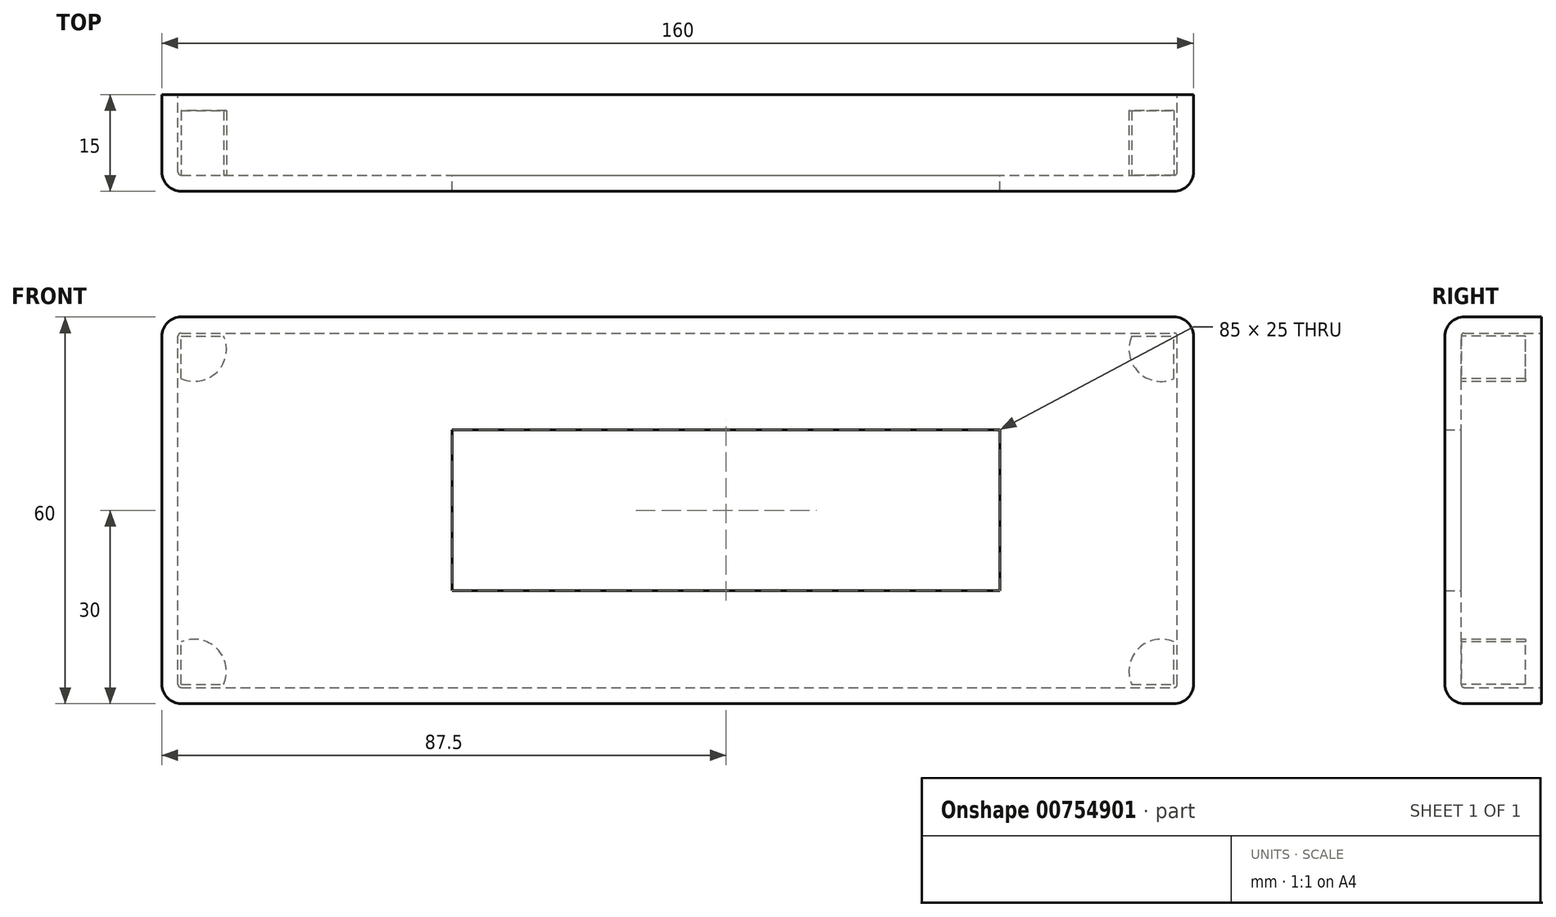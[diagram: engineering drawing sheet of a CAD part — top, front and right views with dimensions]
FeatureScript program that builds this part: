
annotation { "Feature Type Name" : "Feature", "Feature Type Description" : "" }
export const myFeature = defineFeature(function(context is Context, id is Id, definition is map)
    precondition{}
    {
        {
            var Q0;
            Q0=qCreatedBy(makeId("Front.planeOp"),FACE);
            var sketch = newSketch(context, id + "F0", { "sketchPlane" : qUnion([Q0])});
            skLineSegment(sketch, "E0.bottom", {"start": v(0, 0) * mm, "end": v(160, 0) * mm});
            skLineSegment(sketch, "E0.top", {"start": v(0, 60) * mm, "end": v(160, 60) * mm});
            skLineSegment(sketch, "E0.left", {"start": v(0, 0) * mm, "end": v(0, 60) * mm});
            skLineSegment(sketch, "E0.right", {"start": v(160, 0) * mm, "end": v(160, 60) * mm});
            skSolve(sketch);
        }
        {
            var Q0;
            Q0=makeQuery(id+"F0.imprint","IMPRINT",FACE,{"disambiguationData":[TD([[makeQuery(id+"F0.imprint","IMPRINT",EDGE,{"derivedFrom":sQuery(id+"F0.wireOp",EDGE,"E0.bottom")}),1.0]])]});
            extrude(context, id + "F1", {"entities" : qUnion([Q0]), "depth" : 15 * mm, "offsetDistance" : 25 * mm});
        }
        {
            var Q0;
            Q0=makeQuery(id+"F1.opExtrude","SWEPT_EDGE",EDGE,{"disambiguationData":[OSD([sQuery(id+"F0.wireOp",EDGE,"E0.top"),sQuery(id+"F0.wireOp",EDGE,"E0.left")])]});
            var Q1;
            Q1=makeQuery(id+"F1.opExtrude","CAP_EDGE",EDGE,{"disambiguationData":[OSD([sQuery(id+"F0.wireOp",EDGE,"E0.top")])],"isStart":false});
            var Q2;
            Q2=makeQuery(id+"F1.opExtrude","CAP_EDGE",EDGE,{"disambiguationData":[OSD([sQuery(id+"F0.wireOp",EDGE,"E0.left")])],"isStart":false});
            var Q3;
            Q3=makeQuery(id+"F1.opExtrude","CAP_EDGE",EDGE,{"disambiguationData":[OSD([sQuery(id+"F0.wireOp",EDGE,"E0.bottom")])],"isStart":false});
            var Q4;
            Q4=makeQuery(id+"F1.opExtrude","SWEPT_EDGE",EDGE,{"disambiguationData":[OSD([sQuery(id+"F0.wireOp",EDGE,"E0.bottom"),sQuery(id+"F0.wireOp",EDGE,"E0.left")])]});
            var Q5;
            Q5=makeQuery(id+"F1.opExtrude","SWEPT_EDGE",EDGE,{"disambiguationData":[OSD([sQuery(id+"F0.wireOp",EDGE,"E0.bottom"),sQuery(id+"F0.wireOp",EDGE,"E0.right")])]});
            var Q6;
            Q6=makeQuery(id+"F1.opExtrude","SWEPT_EDGE",EDGE,{"disambiguationData":[OSD([sQuery(id+"F0.wireOp",EDGE,"E0.top"),sQuery(id+"F0.wireOp",EDGE,"E0.right")])]});
            var Q7;
            Q7=makeQuery(id+"F1.opExtrude","CAP_EDGE",EDGE,{"disambiguationData":[OSD([sQuery(id+"F0.wireOp",EDGE,"E0.right")])],"isStart":false});
            fillet(context, id + "F2", {"entities" : qUnion([Q0, Q1, Q2, Q3, Q4, Q5, Q6, Q7]), "radius" : 3 * mm, "tangentPropagation" : true, "allowEdgeOverflow" : false});
        }
        {
            var Q0;
            Q0=makeQuery(id+"F1.opExtrude","CAP_FACE",FACE,{"disambiguationData":[OSD([sQuery(id+"F0.wireOp",EDGE,"E0.bottom"),sQuery(id+"F0.wireOp",EDGE,"E0.top"),sQuery(id+"F0.wireOp",EDGE,"E0.left"),sQuery(id+"F0.wireOp",EDGE,"E0.right")])],"isStart":true});
            shell(context, id + "F3", {"entities" : qUnion([Q0]), "thickness" : 2.5 * mm});
        }
        {
            var Q0;
            Q0=makeQuery(id+"F3.opShell","OFFSET_FACE",FACE,{"disambiguationData":[OSD([sQuery(id+"F0.wireOp",EDGE,"E0.bottom"),sQuery(id+"F0.wireOp",EDGE,"E0.top"),sQuery(id+"F0.wireOp",EDGE,"E0.left"),sQuery(id+"F0.wireOp",EDGE,"E0.right")])]});
            var sketch = newSketch(context, id + "F4", { "sketchPlane" : qUnion([Q0])});
            skCircle(sketch, "E1", {"center": v(-155, 55) * mm, "radius": 5 * mm});
            skCircle(sketch, "E2", {"center": v(-155, 5) * mm, "radius": 5 * mm});
            skCircle(sketch, "E3", {"center": v(-5, 55) * mm, "radius": 5 * mm});
            skCircle(sketch, "E4", {"center": v(-5, 5) * mm, "radius": 5 * mm});
            skSolve(sketch);
        }
        {
            var Q0;
            {var subQ0=sQuery(id+"F4.wireOp",EDGE,"E1");var subQ1=sQuery(id+"F0.wireOp",EDGE,"E0.right");var subQ2=sQuery(id+"F0.wireOp",EDGE,"E0.left");var subQ3=sQuery(id+"F0.wireOp",EDGE,"E0.top");var subQ4=sQuery(id+"F0.wireOp",EDGE,"E0.bottom");var subQ5=makeQuery(id+"F1.opExtrude","CAP_FACE",FACE,{"disambiguationData":[OSD([subQ4,subQ3,subQ2,subQ1])],"isStart":false});var subQ6=makeQuery(id+"F3.opShell","OFFSET_EDGE",EDGE,{"disambiguationData":[OSD([subQ4,subQ3,subQ2,subQ1]),TDD([makeQuery(id+"F2.opFillet","BLEND_EDGE",EDGE,{"blendedFrom":[makeQuery(id+"F1.opExtrude","CAP_EDGE",EDGE,{"disambiguationData":[OSD([subQ3])],"isStart":false}),subQ5],"blendedInto":[subQ5]})])]});var subQ7=makeQuery(id+"F4.imprint","INTERSECT",VERTEX,{"derivedFrom":[subQ6,subQ0]});Q0=makeQuery(id+"F4.imprint","IMPRINT",FACE,{"disambiguationData":[TD([[makeQuery(id+"F4.imprint","IMPRINT",EDGE,{"disambiguationData":[TD([[subQ7,1.0]])],"derivedFrom":subQ0}),1.0]])]});}
            var Q1;
            {var subQ0=sQuery(id+"F4.wireOp",EDGE,"E2");var subQ1=sQuery(id+"F0.wireOp",EDGE,"E0.right");var subQ2=sQuery(id+"F0.wireOp",EDGE,"E0.left");var subQ3=sQuery(id+"F0.wireOp",EDGE,"E0.top");var subQ4=sQuery(id+"F0.wireOp",EDGE,"E0.bottom");var subQ5=makeQuery(id+"F1.opExtrude","CAP_FACE",FACE,{"disambiguationData":[OSD([subQ4,subQ3,subQ2,subQ1])],"isStart":false});var subQ6=makeQuery(id+"F3.opShell","OFFSET_EDGE",EDGE,{"disambiguationData":[OSD([subQ4,subQ3,subQ2,subQ1]),TDD([makeQuery(id+"F2.opFillet","BLEND_EDGE",EDGE,{"blendedFrom":[makeQuery(id+"F1.opExtrude","CAP_EDGE",EDGE,{"disambiguationData":[OSD([subQ4])],"isStart":false}),subQ5],"blendedInto":[subQ5]})])]});var subQ7=makeQuery(id+"F4.imprint","INTERSECT",VERTEX,{"derivedFrom":[subQ6,subQ0]});Q1=makeQuery(id+"F4.imprint","IMPRINT",FACE,{"disambiguationData":[TD([[makeQuery(id+"F4.imprint","IMPRINT",EDGE,{"disambiguationData":[TD([[subQ7,-1.0]])],"derivedFrom":subQ0}),1.0]])]});}
            var Q2;
            {var subQ0=sQuery(id+"F4.wireOp",EDGE,"E3");var subQ1=sQuery(id+"F0.wireOp",EDGE,"E0.right");var subQ2=sQuery(id+"F0.wireOp",EDGE,"E0.left");var subQ3=sQuery(id+"F0.wireOp",EDGE,"E0.top");var subQ4=sQuery(id+"F0.wireOp",EDGE,"E0.bottom");var subQ5=makeQuery(id+"F1.opExtrude","CAP_FACE",FACE,{"disambiguationData":[OSD([subQ4,subQ3,subQ2,subQ1])],"isStart":false});var subQ6=makeQuery(id+"F3.opShell","OFFSET_EDGE",EDGE,{"disambiguationData":[OSD([subQ4,subQ3,subQ2,subQ1]),TDD([makeQuery(id+"F2.opFillet","BLEND_EDGE",EDGE,{"blendedFrom":[makeQuery(id+"F1.opExtrude","CAP_EDGE",EDGE,{"disambiguationData":[OSD([subQ3])],"isStart":false}),subQ5],"blendedInto":[subQ5]})])]});var subQ7=makeQuery(id+"F4.imprint","INTERSECT",VERTEX,{"derivedFrom":[subQ6,subQ0]});Q2=makeQuery(id+"F4.imprint","IMPRINT",FACE,{"disambiguationData":[TD([[makeQuery(id+"F4.imprint","IMPRINT",EDGE,{"disambiguationData":[TD([[subQ7,-1.0]])],"derivedFrom":subQ0}),1.0]])]});}
            var Q3;
            {var subQ0=sQuery(id+"F4.wireOp",EDGE,"E4");var subQ1=sQuery(id+"F0.wireOp",EDGE,"E0.right");var subQ2=sQuery(id+"F0.wireOp",EDGE,"E0.left");var subQ3=sQuery(id+"F0.wireOp",EDGE,"E0.top");var subQ4=sQuery(id+"F0.wireOp",EDGE,"E0.bottom");var subQ5=makeQuery(id+"F1.opExtrude","CAP_FACE",FACE,{"disambiguationData":[OSD([subQ4,subQ3,subQ2,subQ1])],"isStart":false});var subQ6=makeQuery(id+"F3.opShell","OFFSET_EDGE",EDGE,{"disambiguationData":[OSD([subQ4,subQ3,subQ2,subQ1]),TDD([makeQuery(id+"F2.opFillet","BLEND_EDGE",EDGE,{"blendedFrom":[makeQuery(id+"F1.opExtrude","CAP_EDGE",EDGE,{"disambiguationData":[OSD([subQ4])],"isStart":false}),subQ5],"blendedInto":[subQ5]})])]});var subQ7=makeQuery(id+"F4.imprint","INTERSECT",VERTEX,{"derivedFrom":[subQ6,subQ0]});Q3=makeQuery(id+"F4.imprint","IMPRINT",FACE,{"disambiguationData":[TD([[makeQuery(id+"F4.imprint","IMPRINT",EDGE,{"disambiguationData":[TD([[subQ7,1.0]])],"derivedFrom":subQ0}),1.0]])]});}
            var Q4;
            {var subQ0=sQuery(id+"F4.wireOp",EDGE,"ceb6a8c3-83ea-4a42-8ad1-0d2410ddc587");var subQ1=sQuery(id+"F0.wireOp",EDGE,"E0.right");var subQ2=sQuery(id+"F0.wireOp",EDGE,"E0.left");var subQ3=sQuery(id+"F0.wireOp",EDGE,"E0.top");var subQ4=sQuery(id+"F0.wireOp",EDGE,"E0.bottom");var subQ5=makeQuery(id+"F1.opExtrude","CAP_FACE",FACE,{"disambiguationData":[OSD([subQ4,subQ3,subQ2,subQ1])],"isStart":false});var subQ6=makeQuery(id+"F3.opShell","OFFSET_EDGE",EDGE,{"disambiguationData":[OSD([subQ4,subQ3,subQ2,subQ1]),TDD([makeQuery(id+"F2.opFillet","BLEND_EDGE",EDGE,{"blendedFrom":[makeQuery(id+"F1.opExtrude","CAP_EDGE",EDGE,{"disambiguationData":[OSD([subQ3])],"isStart":false}),subQ5],"blendedInto":[subQ5]})])]});var subQ7=makeQuery(id+"F4.imprint","INTERSECT",VERTEX,{"derivedFrom":[subQ6,subQ0]});Q4=makeQuery(id+"F4.imprint","IMPRINT",FACE,{"disambiguationData":[TD([[makeQuery(id+"F4.imprint","IMPRINT",EDGE,{"disambiguationData":[TD([[subQ7,1.0]])],"derivedFrom":subQ0}),-1.0]])]});}
            var Q5;
            {var subQ0=sQuery(id+"F4.wireOp",EDGE,"14a948d3-5733-4252-9dd9-3c15a1e3127a");var subQ1=sQuery(id+"F0.wireOp",EDGE,"E0.right");var subQ2=sQuery(id+"F0.wireOp",EDGE,"E0.left");var subQ3=sQuery(id+"F0.wireOp",EDGE,"E0.top");var subQ4=sQuery(id+"F0.wireOp",EDGE,"E0.bottom");var subQ5=makeQuery(id+"F1.opExtrude","CAP_FACE",FACE,{"disambiguationData":[OSD([subQ4,subQ3,subQ2,subQ1])],"isStart":false});var subQ6=makeQuery(id+"F3.opShell","OFFSET_EDGE",EDGE,{"disambiguationData":[OSD([subQ4,subQ3,subQ2,subQ1]),TDD([makeQuery(id+"F2.opFillet","BLEND_EDGE",EDGE,{"blendedFrom":[makeQuery(id+"F1.opExtrude","CAP_EDGE",EDGE,{"disambiguationData":[OSD([subQ3])],"isStart":false}),subQ5],"blendedInto":[subQ5]})])]});var subQ7=makeQuery(id+"F4.imprint","INTERSECT",VERTEX,{"derivedFrom":[subQ6,subQ0]});Q5=makeQuery(id+"F4.imprint","IMPRINT",FACE,{"disambiguationData":[TD([[makeQuery(id+"F4.imprint","IMPRINT",EDGE,{"disambiguationData":[TD([[subQ7,-1.0]])],"derivedFrom":subQ0}),-1.0]])]});}
            var Q6;
            {var subQ0=sQuery(id+"F4.wireOp",EDGE,"e6a02f4f-9173-470f-86b5-5cf8c1340213");var subQ1=sQuery(id+"F0.wireOp",EDGE,"E0.right");var subQ2=sQuery(id+"F0.wireOp",EDGE,"E0.left");var subQ3=sQuery(id+"F0.wireOp",EDGE,"E0.top");var subQ4=sQuery(id+"F0.wireOp",EDGE,"E0.bottom");var subQ5=makeQuery(id+"F1.opExtrude","CAP_FACE",FACE,{"disambiguationData":[OSD([subQ4,subQ3,subQ2,subQ1])],"isStart":false});var subQ6=makeQuery(id+"F3.opShell","OFFSET_EDGE",EDGE,{"disambiguationData":[OSD([subQ4,subQ3,subQ2,subQ1]),TDD([makeQuery(id+"F2.opFillet","BLEND_EDGE",EDGE,{"blendedFrom":[makeQuery(id+"F1.opExtrude","CAP_EDGE",EDGE,{"disambiguationData":[OSD([subQ4])],"isStart":false}),subQ5],"blendedInto":[subQ5]})])]});var subQ7=makeQuery(id+"F4.imprint","INTERSECT",VERTEX,{"derivedFrom":[subQ6,subQ0]});Q6=makeQuery(id+"F4.imprint","IMPRINT",FACE,{"disambiguationData":[TD([[makeQuery(id+"F4.imprint","IMPRINT",EDGE,{"disambiguationData":[TD([[subQ7,1.0]])],"derivedFrom":subQ0}),-1.0]])]});}
            var Q7;
            {var subQ0=sQuery(id+"F4.wireOp",EDGE,"3f37ad98-5e16-4e9e-b798-fc5b4a82ff59");var subQ1=sQuery(id+"F0.wireOp",EDGE,"E0.right");var subQ2=sQuery(id+"F0.wireOp",EDGE,"E0.left");var subQ3=sQuery(id+"F0.wireOp",EDGE,"E0.top");var subQ4=sQuery(id+"F0.wireOp",EDGE,"E0.bottom");var subQ5=makeQuery(id+"F1.opExtrude","CAP_FACE",FACE,{"disambiguationData":[OSD([subQ4,subQ3,subQ2,subQ1])],"isStart":false});var subQ6=makeQuery(id+"F3.opShell","OFFSET_EDGE",EDGE,{"disambiguationData":[OSD([subQ4,subQ3,subQ2,subQ1]),TDD([makeQuery(id+"F2.opFillet","BLEND_EDGE",EDGE,{"blendedFrom":[makeQuery(id+"F1.opExtrude","CAP_EDGE",EDGE,{"disambiguationData":[OSD([subQ4])],"isStart":false}),subQ5],"blendedInto":[subQ5]})])]});var subQ7=makeQuery(id+"F4.imprint","INTERSECT",VERTEX,{"derivedFrom":[subQ6,subQ0]});Q7=makeQuery(id+"F4.imprint","IMPRINT",FACE,{"disambiguationData":[TD([[makeQuery(id+"F4.imprint","IMPRINT",EDGE,{"disambiguationData":[TD([[subQ7,-1.0]])],"derivedFrom":subQ0}),-1.0]])]});}
            extrude(context, id + "F5", {"entities" : qUnion([Q0, Q1, Q2, Q3, Q4, Q5, Q6, Q7]), "operationType" : NewBodyOperationType.ADD, "depth" : 10 * mm, "offsetDistance" : 25 * mm});
        }
        {
            var Q0;
            Q0=makeQuery(id+"F3.opShell","OFFSET_FACE",FACE,{"disambiguationData":[OSD([sQuery(id+"F0.wireOp",EDGE,"E0.bottom"),sQuery(id+"F0.wireOp",EDGE,"E0.top"),sQuery(id+"F0.wireOp",EDGE,"E0.left"),sQuery(id+"F0.wireOp",EDGE,"E0.right")])]});
            var sketch = newSketch(context, id + "F6", { "sketchPlane" : qUnion([Q0])});
            skLineSegment(sketch, "E5.bottom", {"start": v(-45, 17.5) * mm, "end": v(-130, 17.5) * mm});
            skLineSegment(sketch, "E5.top", {"start": v(-45, 42.5) * mm, "end": v(-130, 42.5) * mm});
            skLineSegment(sketch, "E5.left", {"start": v(-45, 17.5) * mm, "end": v(-45, 42.5) * mm});
            skLineSegment(sketch, "E5.right", {"start": v(-130, 17.5) * mm, "end": v(-130, 42.5) * mm});
            skSolve(sketch);
        }
        {
            var Q0;
            Q0 = qSketchRegion(id + "F6", true);
            extrude(context, id + "F7", {"entities" : qUnion([Q0]), "operationType" : NewBodyOperationType.REMOVE, "oppositeDirection" : true, "depth" : 25 * mm, "offsetDistance" : 25 * mm});
        }
    });
